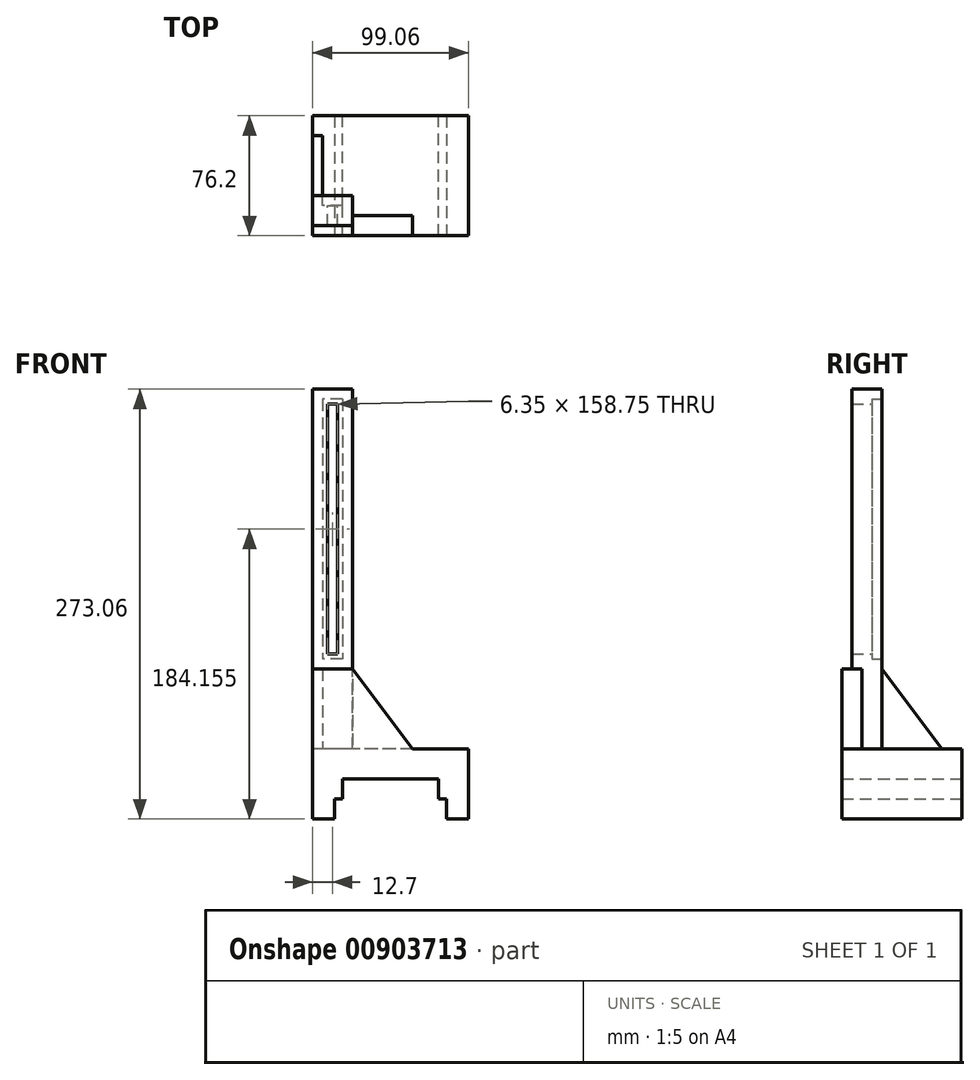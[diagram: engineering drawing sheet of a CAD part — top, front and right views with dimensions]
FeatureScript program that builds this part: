
annotation { "Feature Type Name" : "Feature", "Feature Type Description" : "" }
export const myFeature = defineFeature(function(context is Context, id is Id, definition is map)
    precondition{}
    {
        {
            var Q0;
            Q0=qCreatedBy(makeId("Front.planeOp"),FACE);
            var sketch = newSketch(context, id + "F0", { "sketchPlane" : qUnion([Q0])});
            skLineSegment(sketch, "E0.bottom", {"start": v(49.53, -22.23) * mm, "end": v(-49.53, -22.23) * mm});
            skLineSegment(sketch, "E0.top", {"start": v(49.53, 22.23) * mm, "end": v(-49.53, 22.23) * mm});
            skLineSegment(sketch, "E0.left", {"start": v(49.53, -22.23) * mm, "end": v(49.53, 22.23) * mm});
            skLineSegment(sketch, "E0.right", {"start": v(-49.53, -22.23) * mm, "end": v(-49.53, 22.22) * mm});
            skPoint(sketch, "E0.middle", {"position": v(0, 0) * mm});
            skLineSegment(sketch, "E1.bottom", {"start": v(30.48, -47.63) * mm, "end": v(-30.48, -47.63) * mm});
            skLineSegment(sketch, "E1.top", {"start": v(30.48, 3.18) * mm, "end": v(-30.48, 3.18) * mm});
            skLineSegment(sketch, "E1.left", {"start": v(30.48, -47.63) * mm, "end": v(30.48, 3.18) * mm});
            skLineSegment(sketch, "E1.right", {"start": v(-30.48, -47.63) * mm, "end": v(-30.48, 3.18) * mm});
            skPoint(sketch, "E1.middle", {"position": v(0, -22.23) * mm});
            skSolve(sketch);
        }
        {
            var Q0;
            Q0=makeQuery(id+"F0.imprint","IMPRINT",FACE,{"disambiguationData":[TD([[makeQuery(id+"F0.imprint","IMPRINT",EDGE,{"derivedFrom":sQuery(id+"F0.wireOp",EDGE,"E0.top")}),1.0]])]});
            extrude(context, id + "F1", {"entities" : qUnion([Q0]), "endBound" : BoundingType.SYMMETRIC, "depth" : 76.2 * mm, "offsetDistance" : 25.4 * mm});
        }
        {
            var Q0;
            Q0=qCreatedBy(makeId("Front.planeOp"),FACE);
            var sketch = newSketch(context, id + "F2", { "sketchPlane" : qUnion([Q0])});
            skLineSegment(sketch, "E2.bottom", {"start": v(35.56, -36.92) * mm, "end": v(-35.56, -36.92) * mm});
            skLineSegment(sketch, "E2.top", {"start": v(35.56, -9.52) * mm, "end": v(-35.56, -9.53) * mm});
            skLineSegment(sketch, "E2.left", {"start": v(35.56, -36.92) * mm, "end": v(35.56, -9.53) * mm});
            skLineSegment(sketch, "E2.right", {"start": v(-35.56, -36.92) * mm, "end": v(-35.56, -9.53) * mm});
            skPoint(sketch, "E2.middle", {"position": v(0, -23.22) * mm});
            skSolve(sketch);
        }
        {
            var Q0;
            Q0=makeQuery(id+"F2.imprint","IMPRINT",FACE,{"disambiguationData":[TD([[makeQuery(id+"F2.imprint","IMPRINT",EDGE,{"derivedFrom":sQuery(id+"F2.wireOp",EDGE,"E2.bottom")}),-1.0]])]});
            extrude(context, id + "F3", {"entities" : qUnion([Q0]), "operationType" : NewBodyOperationType.REMOVE, "endBound" : BoundingType.SYMMETRIC, "oppositeDirection" : true, "depth" : 101.6 * mm, "offsetDistance" : 25.4 * mm});
        }
        {
            var Q0;
            Q0=makeQuery(id+"F1.opExtrude","SWEPT_FACE",FACE,{"disambiguationData":[OSD([sQuery(id+"F0.wireOp",EDGE,"E0.top")])]});
            var sketch = newSketch(context, id + "F4", { "sketchPlane" : qUnion([Q0])});
            skPoint(sketch, "E3.right.end.orphan", {"position": v(-7.9, -5.96) * mm});
            skPoint(sketch, "E3.bottom.end.orphan", {"position": v(-7.9, -51.19) * mm});
            skLineSegment(sketch, "E4.bottom", {"start": v(-24.13, -31.75) * mm, "end": v(-49.53, -31.75) * mm});
            skLineSegment(sketch, "E4.top", {"start": v(-24.13, -12.7) * mm, "end": v(-49.53, -12.7) * mm});
            skLineSegment(sketch, "E4.left", {"start": v(-24.13, -31.75) * mm, "end": v(-24.13, -12.7) * mm});
            skLineSegment(sketch, "E4.right", {"start": v(-49.53, -31.75) * mm, "end": v(-49.53, -12.7) * mm});
            skPoint(sketch, "E4.middle", {"position": v(-36.83, -22.23) * mm});
            skSolve(sketch);
        }
        {
            var Q0;
            Q0=qSketchRegion(id+"F4",true);
            extrude(context, id + "F5", {"entities" : qUnion([Q0]), "operationType" : NewBodyOperationType.ADD, "depth" : 228.6 * mm, "offsetDistance" : 25.4 * mm});
        }
        {
            var Q0;
            Q0=makeQuery(id+"F1.opExtrude","CAP_FACE",FACE,{"disambiguationData":[OSD([sQuery(id+"F0.wireOp",EDGE,"E0.bottom"),sQuery(id+"F0.wireOp",EDGE,"E0.top"),sQuery(id+"F0.wireOp",EDGE,"E0.left"),sQuery(id+"F0.wireOp",EDGE,"E0.right"),sQuery(id+"F0.wireOp",EDGE,"E1.top"),sQuery(id+"F0.wireOp",EDGE,"E1.left"),sQuery(id+"F0.wireOp",EDGE,"E1.right")])],"isStart":false});
            var sketch = newSketch(context, id + "F6", { "sketchPlane" : qUnion([Q0])});
            skLineSegment(sketch, "E5.bottom", {"start": v(-49.53, 22.22) * mm, "end": v(-24.13, 22.22) * mm});
            skLineSegment(sketch, "E5.top", {"start": v(-49.53, 73.03) * mm, "end": v(-24.13, 73.03) * mm});
            skLineSegment(sketch, "E5.left", {"start": v(-49.53, 22.22) * mm, "end": v(-49.53, 73.03) * mm});
            skLineSegment(sketch, "E5.right", {"start": v(-24.13, 22.22) * mm, "end": v(-24.13, 73.03) * mm});
            skLineSegment(sketch, "E6", {"start": v(-24.13, 22.22) * mm, "end": v(13.97, 22.23) * mm});
            skLineSegment(sketch, "E7", {"start": v(-24.13, 73.03) * mm, "end": v(13.97, 22.23) * mm});
            skSolve(sketch);
        }
        {
            var Q0;
            Q0 = qSketchRegion(id + "F6", true);
            extrude(context, id + "F7", {"entities" : qUnion([Q0]), "operationType" : NewBodyOperationType.ADD, "oppositeDirection" : true, "depth" : 12.7 * mm, "offsetDistance" : 25.4 * mm});
        }
        {
            var Q0;
            Q0=makeQuery(id+"F7.boolean.opBoolean","MERGE",FACE,{"derivedFrom":[makeQuery(id+"F5.boolean.opBoolean","MERGE",FACE,{"derivedFrom":[makeQuery(id+"F1.opExtrude","SWEPT_FACE",FACE,{"disambiguationData":[OSD([sQuery(id+"F0.wireOp",EDGE,"E0.right")])]}),makeQuery(id+"F5.opExtrude","SWEPT_FACE",FACE,{"disambiguationData":[OSD([sQuery(id+"F4.wireOp",EDGE,"E4.right")])]})]}),makeQuery(id+"F7.opExtrude","SWEPT_FACE",FACE,{"disambiguationData":[OSD([sQuery(id+"F6.wireOp",EDGE,"E5.left")])]})]});
            var sketch = newSketch(context, id + "F8", { "sketchPlane" : qUnion([Q0])});
            skLineSegment(sketch, "E8", {"start": v(12.7, 22.23) * mm, "end": v(-25.4, 22.23) * mm});
            skLineSegment(sketch, "E9", {"start": v(12.7, 22.23) * mm, "end": v(12.7, 73.03) * mm});
            skLineSegment(sketch, "E10", {"start": v(-25.4, 22.22) * mm, "end": v(12.7, 73.03) * mm});
            skSolve(sketch);
        }
        {
            var Q0;
            Q0 = qSketchRegion(id + "F8", true);
            extrude(context, id + "F9", {"entities" : qUnion([Q0]), "operationType" : NewBodyOperationType.ADD, "oppositeDirection" : true, "depth" : 6.35 * mm, "offsetDistance" : 25.4 * mm});
        }
        {
            var Q0;
            Q0=makeQuery(id+"F5.opExtrude","SWEPT_FACE",FACE,{"disambiguationData":[OSD([sQuery(id+"F4.wireOp",EDGE,"E4.top")])]});
            var sketch = newSketch(context, id + "F10", { "sketchPlane" : qUnion([Q0])});
            skLineSegment(sketch, "E11.bottom", {"start": v(30.48, 244.48) * mm, "end": v(43.18, 244.48) * mm});
            skLineSegment(sketch, "E11.top", {"start": v(30.48, 79.38) * mm, "end": v(43.18, 79.38) * mm});
            skLineSegment(sketch, "E11.left", {"start": v(30.48, 244.48) * mm, "end": v(30.48, 79.38) * mm});
            skLineSegment(sketch, "E11.right", {"start": v(43.18, 244.48) * mm, "end": v(43.18, 79.38) * mm});
            skPoint(sketch, "E11.middle", {"position": v(36.83, 161.93) * mm});
            skSolve(sketch);
        }
        {
            var Q0;
            Q0=makeQuery(id+"F10.imprint","IMPRINT",FACE,{"disambiguationData":[TD([[makeQuery(id+"F10.imprint","IMPRINT",EDGE,{"derivedFrom":sQuery(id+"F10.wireOp",EDGE,"E11.bottom")}),-1.0]])]});
            extrude(context, id + "F11", {"entities" : qUnion([Q0]), "operationType" : NewBodyOperationType.REMOVE, "oppositeDirection" : true, "depth" : 6.35 * mm, "offsetDistance" : 25.4 * mm});
        }
        {
            var Q0;
            Q0=makeQuery(id+"F11.boolean.opBoolean","COPY",FACE,{"derivedFrom":makeQuery(id+"F11.opExtrude","CAP_FACE",FACE,{"disambiguationData":[OSD([sQuery(id+"F10.wireOp",EDGE,"E11.bottom"),sQuery(id+"F10.wireOp",EDGE,"E11.top"),sQuery(id+"F10.wireOp",EDGE,"E11.left"),sQuery(id+"F10.wireOp",EDGE,"E11.right")])],"isStart":false})});
            var sketch = newSketch(context, id + "F12", { "sketchPlane" : qUnion([Q0])});
            skLineSegment(sketch, "E12.bottom", {"start": v(40, 241.3) * mm, "end": v(33.66, 241.3) * mm});
            skLineSegment(sketch, "E12.top", {"start": v(40, 82.55) * mm, "end": v(33.66, 82.55) * mm});
            skLineSegment(sketch, "E12.left", {"start": v(40, 241.3) * mm, "end": v(40, 82.55) * mm});
            skLineSegment(sketch, "E12.right", {"start": v(33.66, 241.3) * mm, "end": v(33.66, 82.55) * mm});
            skSolve(sketch);
        }
        {
            var Q0;
            Q0=makeQuery(id+"F12.imprint","IMPRINT",FACE,{"disambiguationData":[TD([[makeQuery(id+"F12.imprint","IMPRINT",EDGE,{"derivedFrom":sQuery(id+"F12.wireOp",EDGE,"E12.bottom")}),1.0]])]});
            extrude(context, id + "F13", {"entities" : qUnion([Q0]), "operationType" : NewBodyOperationType.REMOVE, "oppositeDirection" : true, "depth" : 25.4 * mm, "offsetDistance" : 25.4 * mm});
        }
        {
            var Q0;
            Q0=makeQuery(id+"F5.opExtrude","SWEPT_FACE",FACE,{"disambiguationData":[OSD([sQuery(id+"F4.wireOp",EDGE,"E4.top")])]});
            var sketch = newSketch(context, id + "F14", { "sketchPlane" : qUnion([Q0])});
            skLineSegment(sketch, "E13.bottom", {"start": v(43.18, 263.53) * mm, "end": v(30.48, 263.53) * mm});
            skLineSegment(sketch, "E13.top", {"start": v(43.18, 238.13) * mm, "end": v(30.48, 238.13) * mm});
            skLineSegment(sketch, "E13.left", {"start": v(43.18, 263.53) * mm, "end": v(43.18, 238.13) * mm});
            skLineSegment(sketch, "E13.right", {"start": v(30.48, 263.53) * mm, "end": v(30.48, 238.13) * mm});
            skPoint(sketch, "E13.middle", {"position": v(36.83, 250.83) * mm});
            skSolve(sketch);
        }
        {
            var Q0;
            {var subQ0=sQuery(id+"F14.wireOp",EDGE,"E13.bottom");Q0=makeQuery(id+"F14.imprint","IMPRINT",FACE,{"disambiguationData":[TD([[makeQuery(id+"F14.imprint","IMPRINT",EDGE,{"derivedFrom":subQ0}),1.0]])]});}
            var Q1;
            {var subQ0=sQuery(id+"F14.wireOp",EDGE,"E13.top");Q1=makeQuery(id+"F14.imprint","IMPRINT",FACE,{"disambiguationData":[TD([[makeQuery(id+"F14.imprint","IMPRINT",EDGE,{"derivedFrom":subQ0}),-1.0]])]});}
            var Q2;
            {var subQ1=makeQuery(id+"F11.boolean.opBoolean","COPY",EDGE,{"derivedFrom":makeQuery(id+"F11.opExtrude","CAP_EDGE",EDGE,{"disambiguationData":[OSD([sQuery(id+"F10.wireOp",EDGE,"E11.bottom")])],"isStart":true})});Q2=makeQuery(id+"F14.imprint","IMPRINT",FACE,{"disambiguationData":[TD([[makeQuery(id+"F14.imprint","IMPRINT",EDGE,{"derivedFrom":subQ1}),1.0]])]});}
            extrude(context, id + "F15", {"entities" : qUnion([Q0, Q1, Q2]), "operationType" : NewBodyOperationType.REMOVE, "oppositeDirection" : true, "depth" : 6.35 * mm, "offsetDistance" : 25.4 * mm});
        }
    });
